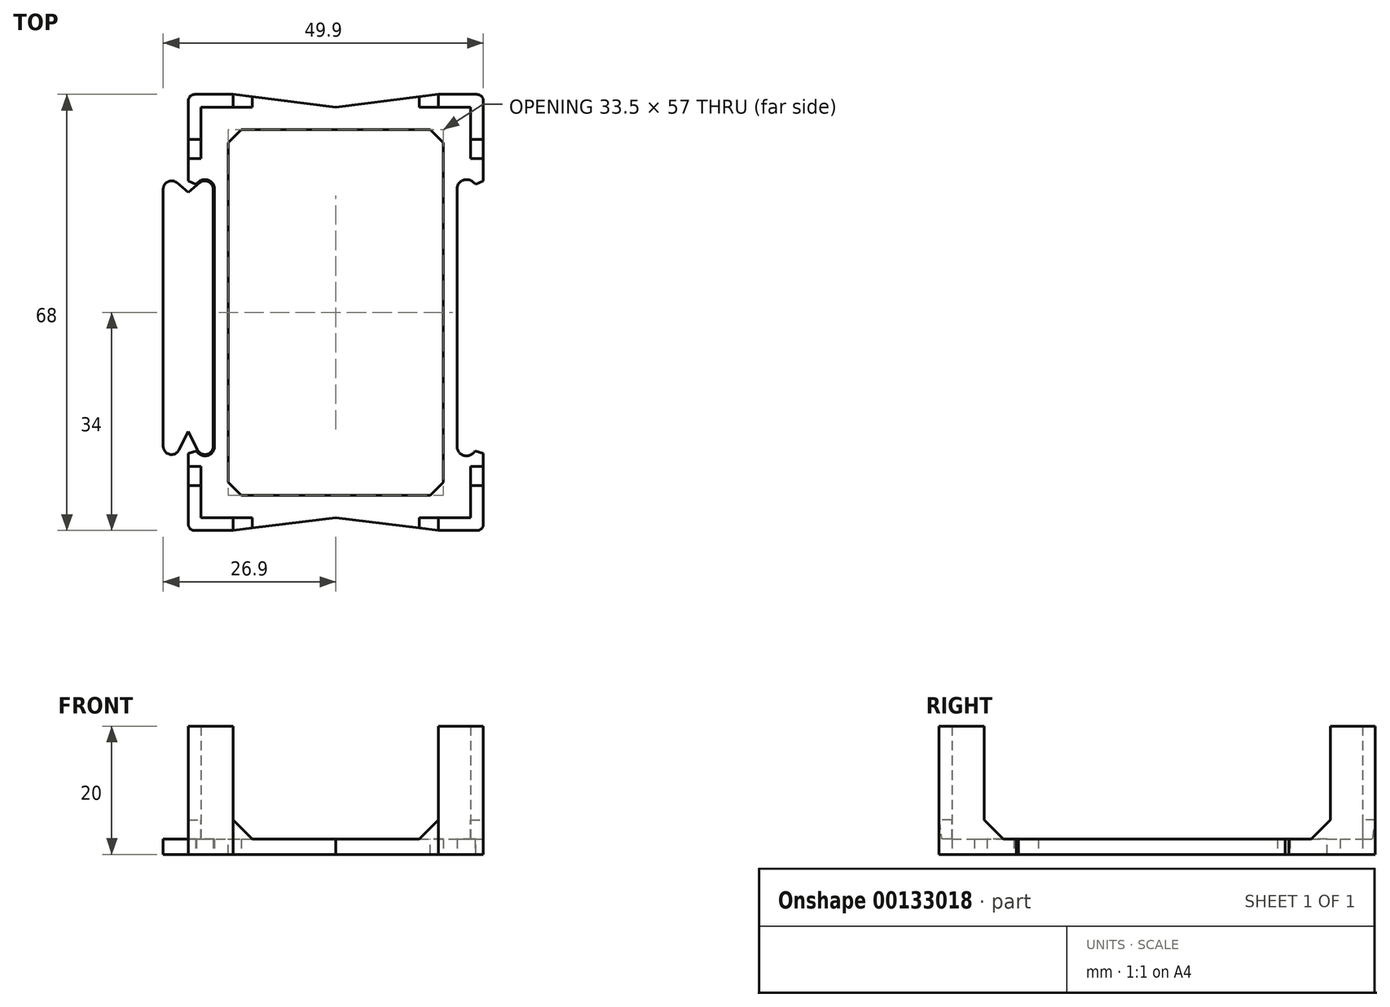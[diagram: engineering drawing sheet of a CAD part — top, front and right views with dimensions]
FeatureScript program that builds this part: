
annotation { "Feature Type Name" : "Feature", "Feature Type Description" : "" }
export const myFeature = defineFeature(function(context is Context, id is Id, definition is map)
    precondition{}
    {
        {
            var Q0;
            Q0=qCreatedBy(makeId("Top.planeOp"),FACE);
            var sketch = newSketch(context, id + "F0", { "sketchPlane" : qUnion([Q0])});
            skLineSegment(sketch, "E0.bottom", {"start": v(21, 32) * mm, "end": v(16, 32) * mm});
            skLineSegment(sketch, "E0.top", {"start": v(21, -32) * mm, "end": v(16, -32) * mm});
            skLineSegment(sketch, "E0.left", {"start": v(21, 32) * mm, "end": v(21, 27) * mm});
            skLineSegment(sketch, "E0.right", {"start": v(-21, 32) * mm, "end": v(-21, 27) * mm});
            skLineSegment(sketch, "E1", {"start": v(-16, 34) * mm, "end": v(-23, 34) * mm});
            skLineSegment(sketch, "E2", {"start": v(-23, 34) * mm, "end": v(-23, 27) * mm});
            skLineSegment(sketch, "E3", {"start": v(-16, 32) * mm, "end": v(-16, 34) * mm});
            skLineSegment(sketch, "E4", {"start": v(-21, 27) * mm, "end": v(-23, 27) * mm});
            skLineSegment(sketch, "E5", {"start": v(16, 34) * mm, "end": v(16, 32) * mm});
            skLineSegment(sketch, "E6", {"start": v(16, 34) * mm, "end": v(23, 34) * mm});
            skLineSegment(sketch, "E7", {"start": v(23, 27) * mm, "end": v(23, 34) * mm});
            skLineSegment(sketch, "E8", {"start": v(21, 27) * mm, "end": v(23, 27) * mm});
            skLineSegment(sketch, "E9", {"start": v(-23, -27) * mm, "end": v(-21, -27) * mm});
            skLineSegment(sketch, "E10", {"start": v(-23, -27) * mm, "end": v(-23, -34) * mm});
            skLineSegment(sketch, "E11", {"start": v(-16, -34) * mm, "end": v(-23, -34) * mm});
            skLineSegment(sketch, "E12", {"start": v(-16, -32) * mm, "end": v(-16, -34) * mm});
            skLineSegment(sketch, "E13", {"start": v(16, -32) * mm, "end": v(16, -34) * mm});
            skLineSegment(sketch, "E14", {"start": v(16, -34) * mm, "end": v(23, -34) * mm});
            skLineSegment(sketch, "E15", {"start": v(23, -27) * mm, "end": v(23, -34) * mm});
            skLineSegment(sketch, "E16", {"start": v(21, -27) * mm, "end": v(23, -27) * mm});
            skLineSegment(sketch, "E17", {"start": v(-16.75, 28.5) * mm, "end": v(16.75, 28.5) * mm});
            skLineSegment(sketch, "E18", {"start": v(16.75, -28.5) * mm, "end": v(-16.75, -28.5) * mm});
            skLineSegment(sketch, "E19", {"start": v(-16.75, 28.5) * mm, "end": v(-16.75, -28.5) * mm});
            skLineSegment(sketch, "E20", {"start": v(16.75, 28.5) * mm, "end": v(16.75, -28.5) * mm});
            skLineSegment(sketch, "E21", {"start": v(-16, 34) * mm, "end": v(0, 32) * mm});
            skLineSegment(sketch, "E22", {"start": v(0, 32) * mm, "end": v(16, 34) * mm});
            skLineSegment(sketch, "E23", {"start": v(-16, -34) * mm, "end": v(0, -32) * mm});
            skLineSegment(sketch, "E24", {"start": v(0, -32) * mm, "end": v(16, -34) * mm});
            skLineSegment(sketch, "E25.trimOffspring", {"start": v(21, -27) * mm, "end": v(21, -32) * mm});
            skLineSegment(sketch, "E26.trimOffspring", {"start": v(-16, -32) * mm, "end": v(-21, -32) * mm});
            skLineSegment(sketch, "E27.trimOffspring", {"start": v(-21, -27) * mm, "end": v(-21, -32) * mm});
            skLineSegment(sketch, "E28", {"start": v(-16, 32) * mm, "end": v(-21, 32) * mm});
            skPoint(sketch, "E29", {"position": v(0, 28.5) * mm});
            skPoint(sketch, "E30", {"position": v(0, -28.5) * mm});
            skPoint(sketch, "E31", {"position": v(-16.75, 0) * mm});
            skPoint(sketch, "E32", {"position": v(16.75, 0) * mm});
            skLineSegment(sketch, "E33", {"start": v(-23, 27) * mm, "end": v(-23, -27) * mm});
            skLineSegment(sketch, "E34", {"start": v(23, -27) * mm, "end": v(23, 27) * mm});
            skLineSegment(sketch, "E35", {"start": v(-23, 19) * mm, "end": v(-21.36, 20.37) * mm});
            skLineSegment(sketch, "E36", {"start": v(-18.9, 19.22) * mm, "end": v(-18.9, -20.86) * mm});
            skLineSegment(sketch, "E37", {"start": v(-21.74, -21.53) * mm, "end": v(-23, -19) * mm});
            skPoint(sketch, "E38.visualSharp", {"position": v(-18.9, 22.44) * mm});
            skArc(sketch, "E38.filletArc", {"start": v(-18.9, 19.22) * mm, "mid": v(-19.76, 20.58) * mm, "end": v(-21.36, 20.37) * mm});
            skPoint(sketch, "E39.visualSharp", {"position": v(-18.9, -27.23) * mm});
            skArc(sketch, "E39.filletArc", {"start": v(-21.74, -21.53) * mm, "mid": v(-20.06, -22.32) * mm, "end": v(-18.9, -20.86) * mm});
            skLineSegment(sketch, "E40.MirrorCS", {"start": v(-23, 19) * mm, "end": v(-24.64, 20.37) * mm});
            skArc(sketch, "E41.MirrorCS", {"start": v(-27.1, 19.22) * mm, "mid": v(-26.24, 20.58) * mm, "end": v(-24.64, 20.37) * mm});
            skLineSegment(sketch, "E42.MirrorCS", {"start": v(-27.1, 19.22) * mm, "end": v(-27.1, -20.86) * mm});
            skArc(sketch, "E43.MirrorCS", {"start": v(-24.26, -21.53) * mm, "mid": v(-25.94, -22.32) * mm, "end": v(-27.1, -20.86) * mm});
            skLineSegment(sketch, "E44.MirrorCS", {"start": v(-24.26, -21.53) * mm, "end": v(-23, -19) * mm});
            skLineSegment(sketch, "E45", {"start": v(0, 40.79) * mm, "end": v(0, -39.35) * mm, "construction": true});
            skLineSegment(sketch, "E46.MirrorCS", {"start": v(18.9, 19.22) * mm, "end": v(18.9, -20.86) * mm});
            skArc(sketch, "E47.MirrorCS", {"start": v(18.9, 19.22) * mm, "mid": v(19.76, 20.58) * mm, "end": v(21.36, 20.37) * mm});
            skLineSegment(sketch, "E48.MirrorCS", {"start": v(23, 19) * mm, "end": v(21.36, 20.37) * mm});
            skLineSegment(sketch, "E49.MirrorCS", {"start": v(23, 19) * mm, "end": v(24.64, 20.37) * mm});
            skArc(sketch, "E50.MirrorCS", {"start": v(27.1, 19.22) * mm, "mid": v(26.24, 20.58) * mm, "end": v(24.64, 20.37) * mm});
            skLineSegment(sketch, "E51.MirrorCS", {"start": v(27.1, 19.22) * mm, "end": v(27.1, -20.86) * mm});
            skArc(sketch, "E52.MirrorCS", {"start": v(24.26, -21.53) * mm, "mid": v(25.94, -22.32) * mm, "end": v(27.1, -20.86) * mm});
            skLineSegment(sketch, "E53.MirrorCS", {"start": v(24.26, -21.53) * mm, "end": v(23, -19) * mm});
            skLineSegment(sketch, "E54.MirrorCS", {"start": v(21.74, -21.53) * mm, "end": v(23, -19) * mm});
            skArc(sketch, "E55.MirrorCS", {"start": v(21.74, -21.53) * mm, "mid": v(20.06, -22.32) * mm, "end": v(18.9, -20.86) * mm});
            skArc(sketch, "E56.0", {"start": v(-19.1, 19.22) * mm, "mid": v(-19.85, 20.4) * mm, "end": v(-21.23, 20.22) * mm});
            skLineSegment(sketch, "E56.1", {"start": v(-23, 18.74) * mm, "end": v(-21.23, 20.22) * mm});
            skLineSegment(sketch, "E56.2", {"start": v(-19.1, 19.22) * mm, "end": v(-19.1, -20.86) * mm});
            skLineSegment(sketch, "E56.3", {"start": v(-23, 18.74) * mm, "end": v(-24.77, 20.22) * mm});
            skArc(sketch, "E56.4", {"start": v(-26.9, 19.22) * mm, "mid": v(-26.15, 20.4) * mm, "end": v(-24.77, 20.22) * mm});
            skLineSegment(sketch, "E56.5", {"start": v(-26.9, 19.22) * mm, "end": v(-26.9, -20.86) * mm});
            skArc(sketch, "E56.6", {"start": v(-21.56, -21.44) * mm, "mid": v(-20.1, -22.12) * mm, "end": v(-19.1, -20.86) * mm});
            skLineSegment(sketch, "E56.7", {"start": v(-21.56, -21.44) * mm, "end": v(-23, -18.55) * mm});
            skLineSegment(sketch, "E56.8", {"start": v(-24.44, -21.44) * mm, "end": v(-23, -18.55) * mm});
            skArc(sketch, "E56.9", {"start": v(-24.44, -21.44) * mm, "mid": v(-25.9, -22.12) * mm, "end": v(-26.9, -20.86) * mm});
            skLineSegment(sketch, "E57.0", {"start": v(-23.9, 19.22) * mm, "end": v(-23.9, -20.86) * mm});
            skSolve(sketch);
        }
        {
            var Q0;
            {var subQ0=sQuery(id+"F0.wireOp",EDGE,"E0.left");var subQ3=sQuery(id+"F0.wireOp",EDGE,"E0.bottom");var subQ4=makeQuery(id+"F0.imprint","INTERSECT",VERTEX,{"derivedFrom":[subQ3,subQ0]});Q0=makeQuery(id+"F0.imprint","IMPRINT",FACE,{"disambiguationData":[TD([[makeQuery(id+"F0.imprint","IMPRINT",EDGE,{"disambiguationData":[TD([[subQ4,-1.0]])],"derivedFrom":subQ3}),1.0]])]});}
            var Q1;
            {var subQ0=sQuery(id+"F0.wireOp",EDGE,"E5");Q1=makeQuery(id+"F0.imprint","IMPRINT",FACE,{"disambiguationData":[TD([[makeQuery(id+"F0.imprint","IMPRINT",EDGE,{"derivedFrom":subQ0}),-1.0]])]});}
            var Q2;
            {var subQ4=sQuery(id+"F0.wireOp",EDGE,"E5");Q2=makeQuery(id+"F0.imprint","IMPRINT",FACE,{"disambiguationData":[TD([[makeQuery(id+"F0.imprint","IMPRINT",EDGE,{"derivedFrom":subQ4}),1.0]])]});}
            var Q3;
            {var subQ0=sQuery(id+"F0.wireOp",EDGE,"E8");Q3=makeQuery(id+"F0.imprint","IMPRINT",FACE,{"disambiguationData":[TD([[makeQuery(id+"F0.imprint","IMPRINT",EDGE,{"derivedFrom":subQ0}),-1.0]])]});}
            var Q4;
            {var subQ0=sQuery(id+"F0.wireOp",EDGE,"E16");Q4=makeQuery(id+"F0.imprint","IMPRINT",FACE,{"disambiguationData":[TD([[makeQuery(id+"F0.imprint","IMPRINT",EDGE,{"derivedFrom":subQ0}),1.0]])]});}
            var Q5;
            {var subQ0=sQuery(id+"F0.wireOp",EDGE,"E13");Q5=makeQuery(id+"F0.imprint","IMPRINT",FACE,{"disambiguationData":[TD([[makeQuery(id+"F0.imprint","IMPRINT",EDGE,{"derivedFrom":subQ0}),1.0]])]});}
            var Q6;
            {var subQ0=sQuery(id+"F0.wireOp",EDGE,"E13");Q6=makeQuery(id+"F0.imprint","IMPRINT",FACE,{"disambiguationData":[TD([[makeQuery(id+"F0.imprint","IMPRINT",EDGE,{"derivedFrom":subQ0}),-1.0]])]});}
            var Q7;
            {var subQ0=sQuery(id+"F0.wireOp",EDGE,"E12");Q7=makeQuery(id+"F0.imprint","IMPRINT",FACE,{"disambiguationData":[TD([[makeQuery(id+"F0.imprint","IMPRINT",EDGE,{"derivedFrom":subQ0}),1.0]])]});}
            var Q8;
            {var subQ4=sQuery(id+"F0.wireOp",EDGE,"E9");Q8=makeQuery(id+"F0.imprint","IMPRINT",FACE,{"disambiguationData":[TD([[makeQuery(id+"F0.imprint","IMPRINT",EDGE,{"derivedFrom":subQ4}),-1.0]])]});}
            var Q9;
            {var subQ0=sQuery(id+"F0.wireOp",EDGE,"E9");Q9=makeQuery(id+"F0.imprint","IMPRINT",FACE,{"disambiguationData":[TD([[makeQuery(id+"F0.imprint","IMPRINT",EDGE,{"derivedFrom":subQ0}),1.0]])]});}
            var Q10;
            {var subQ0=sQuery(id+"F0.wireOp",EDGE,"E4");Q10=makeQuery(id+"F0.imprint","IMPRINT",FACE,{"disambiguationData":[TD([[makeQuery(id+"F0.imprint","IMPRINT",EDGE,{"derivedFrom":subQ0}),1.0]])]});}
            var Q11;
            Q11=makeQuery(id+"F0.imprint","IMPRINT",FACE,{"disambiguationData":[TD([[makeQuery(id+"F0.imprint","IMPRINT",EDGE,{"derivedFrom":sQuery(id+"F0.wireOp",EDGE,"E1")}),1.0]])]});
            var Q12;
            {var subQ0=sQuery(id+"F0.wireOp",EDGE,"E3");Q12=makeQuery(id+"F0.imprint","IMPRINT",FACE,{"disambiguationData":[TD([[makeQuery(id+"F0.imprint","IMPRINT",EDGE,{"derivedFrom":subQ0}),-1.0]])]});}
            extrude(context, id + "F1", {"entities" : qUnion([Q0, Q1, Q2, Q3, Q4, Q5, Q6, Q7, Q8, Q9, Q10, Q11, Q12]), "depth" : 2.4 * mm});
        }
        {
            var Q0;
            Q0=makeQuery(id+"F0.imprint","IMPRINT",FACE,{"disambiguationData":[TD([[makeQuery(id+"F0.imprint","IMPRINT",EDGE,{"derivedFrom":sQuery(id+"F0.wireOp",EDGE,"E1")}),1.0]])]});
            var Q1;
            {var subQ4=sQuery(id+"F0.wireOp",EDGE,"E5");Q1=makeQuery(id+"F0.imprint","IMPRINT",FACE,{"disambiguationData":[TD([[makeQuery(id+"F0.imprint","IMPRINT",EDGE,{"derivedFrom":subQ4}),1.0]])]});}
            var Q2;
            {var subQ0=sQuery(id+"F0.wireOp",EDGE,"E13");Q2=makeQuery(id+"F0.imprint","IMPRINT",FACE,{"disambiguationData":[TD([[makeQuery(id+"F0.imprint","IMPRINT",EDGE,{"derivedFrom":subQ0}),1.0]])]});}
            var Q3;
            {var subQ3=sQuery(id+"F0.wireOp",EDGE,"E9");Q3=makeQuery(id+"F0.imprint","IMPRINT",FACE,{"disambiguationData":[TD([[makeQuery(id+"F0.imprint","IMPRINT",EDGE,{"derivedFrom":subQ3}),-1.0]])]});}
            extrude(context, id + "F2", {"entities" : qUnion([Q0, Q1, Q2, Q3]), "operationType" : NewBodyOperationType.ADD, "depth" : 20 * mm});
        }
        {
            var Q0;
            Q0=makeQuery(id+"F2.boolean.opBoolean","INTERSECT",EDGE,{"derivedFrom":[makeQuery(id+"F1.opExtrude","CAP_FACE",FACE,{"disambiguationData":[OSD([sQuery(id+"F0.wireOp",EDGE,"E1"),sQuery(id+"F0.wireOp",EDGE,"E2"),sQuery(id+"F0.wireOp",EDGE,"E6"),sQuery(id+"F0.wireOp",EDGE,"E7"),sQuery(id+"F0.wireOp",EDGE,"E10"),sQuery(id+"F0.wireOp",EDGE,"E11"),sQuery(id+"F0.wireOp",EDGE,"E14"),sQuery(id+"F0.wireOp",EDGE,"E15"),sQuery(id+"F0.wireOp",EDGE,"E17"),sQuery(id+"F0.wireOp",EDGE,"E18"),sQuery(id+"F0.wireOp",EDGE,"E19"),sQuery(id+"F0.wireOp",EDGE,"E20"),sQuery(id+"F0.wireOp",EDGE,"jiaWZDtS-R24L-EVNI-qtd6-zTstN88FOwR1"),sQuery(id+"F0.wireOp",EDGE,"sGljjnvT-gn0O-4xuL-FiDi-xVXoTiZH4aIa"),sQuery(id+"F0.wireOp",EDGE,"JoJTnnvT-VXK7-kJcO-3MJ3-lJnIAB2w7SyZ"),sQuery(id+"F0.wireOp",EDGE,"D99VeNCh-oXrI-DHgS-fi0i-UPG9c3mJZdQb"),sQuery(id+"F0.wireOp",EDGE,"E21"),sQuery(id+"F0.wireOp",EDGE,"E22"),sQuery(id+"F0.wireOp",EDGE,"E23"),sQuery(id+"F0.wireOp",EDGE,"E24")])],"isStart":false}),makeQuery(id+"F2.opExtrude","SWEPT_FACE",FACE,{"disambiguationData":[OSD([sQuery(id+"F0.wireOp",EDGE,"E4")])]})]});
            var Q1;
            Q1=makeQuery(id+"F2.boolean.opBoolean","INTERSECT",EDGE,{"derivedFrom":[makeQuery(id+"F1.opExtrude","CAP_FACE",FACE,{"disambiguationData":[OSD([sQuery(id+"F0.wireOp",EDGE,"E1"),sQuery(id+"F0.wireOp",EDGE,"E2"),sQuery(id+"F0.wireOp",EDGE,"E6"),sQuery(id+"F0.wireOp",EDGE,"E7"),sQuery(id+"F0.wireOp",EDGE,"E10"),sQuery(id+"F0.wireOp",EDGE,"E11"),sQuery(id+"F0.wireOp",EDGE,"E14"),sQuery(id+"F0.wireOp",EDGE,"E15"),sQuery(id+"F0.wireOp",EDGE,"E17"),sQuery(id+"F0.wireOp",EDGE,"E18"),sQuery(id+"F0.wireOp",EDGE,"E19"),sQuery(id+"F0.wireOp",EDGE,"E20"),sQuery(id+"F0.wireOp",EDGE,"jiaWZDtS-R24L-EVNI-qtd6-zTstN88FOwR1"),sQuery(id+"F0.wireOp",EDGE,"sGljjnvT-gn0O-4xuL-FiDi-xVXoTiZH4aIa"),sQuery(id+"F0.wireOp",EDGE,"JoJTnnvT-VXK7-kJcO-3MJ3-lJnIAB2w7SyZ"),sQuery(id+"F0.wireOp",EDGE,"D99VeNCh-oXrI-DHgS-fi0i-UPG9c3mJZdQb"),sQuery(id+"F0.wireOp",EDGE,"E21"),sQuery(id+"F0.wireOp",EDGE,"E22"),sQuery(id+"F0.wireOp",EDGE,"E23"),sQuery(id+"F0.wireOp",EDGE,"E24")])],"isStart":false}),makeQuery(id+"F2.opExtrude","SWEPT_FACE",FACE,{"disambiguationData":[OSD([sQuery(id+"F0.wireOp",EDGE,"E3")])]})]});
            var Q2;
            Q2=makeQuery(id+"F2.boolean.opBoolean","INTERSECT",EDGE,{"derivedFrom":[makeQuery(id+"F1.opExtrude","CAP_FACE",FACE,{"disambiguationData":[OSD([sQuery(id+"F0.wireOp",EDGE,"E1"),sQuery(id+"F0.wireOp",EDGE,"E2"),sQuery(id+"F0.wireOp",EDGE,"E6"),sQuery(id+"F0.wireOp",EDGE,"E7"),sQuery(id+"F0.wireOp",EDGE,"E10"),sQuery(id+"F0.wireOp",EDGE,"E11"),sQuery(id+"F0.wireOp",EDGE,"E14"),sQuery(id+"F0.wireOp",EDGE,"E15"),sQuery(id+"F0.wireOp",EDGE,"E17"),sQuery(id+"F0.wireOp",EDGE,"E18"),sQuery(id+"F0.wireOp",EDGE,"E19"),sQuery(id+"F0.wireOp",EDGE,"E20"),sQuery(id+"F0.wireOp",EDGE,"jiaWZDtS-R24L-EVNI-qtd6-zTstN88FOwR1"),sQuery(id+"F0.wireOp",EDGE,"sGljjnvT-gn0O-4xuL-FiDi-xVXoTiZH4aIa"),sQuery(id+"F0.wireOp",EDGE,"JoJTnnvT-VXK7-kJcO-3MJ3-lJnIAB2w7SyZ"),sQuery(id+"F0.wireOp",EDGE,"D99VeNCh-oXrI-DHgS-fi0i-UPG9c3mJZdQb"),sQuery(id+"F0.wireOp",EDGE,"E21"),sQuery(id+"F0.wireOp",EDGE,"E22"),sQuery(id+"F0.wireOp",EDGE,"E23"),sQuery(id+"F0.wireOp",EDGE,"E24")])],"isStart":false}),makeQuery(id+"F2.opExtrude","SWEPT_FACE",FACE,{"disambiguationData":[OSD([sQuery(id+"F0.wireOp",EDGE,"E8")])]})]});
            var Q3;
            Q3=makeQuery(id+"F2.boolean.opBoolean","INTERSECT",EDGE,{"derivedFrom":[makeQuery(id+"F1.opExtrude","CAP_FACE",FACE,{"disambiguationData":[OSD([sQuery(id+"F0.wireOp",EDGE,"E1"),sQuery(id+"F0.wireOp",EDGE,"E2"),sQuery(id+"F0.wireOp",EDGE,"E6"),sQuery(id+"F0.wireOp",EDGE,"E7"),sQuery(id+"F0.wireOp",EDGE,"E10"),sQuery(id+"F0.wireOp",EDGE,"E11"),sQuery(id+"F0.wireOp",EDGE,"E14"),sQuery(id+"F0.wireOp",EDGE,"E15"),sQuery(id+"F0.wireOp",EDGE,"E17"),sQuery(id+"F0.wireOp",EDGE,"E18"),sQuery(id+"F0.wireOp",EDGE,"E19"),sQuery(id+"F0.wireOp",EDGE,"E20"),sQuery(id+"F0.wireOp",EDGE,"jiaWZDtS-R24L-EVNI-qtd6-zTstN88FOwR1"),sQuery(id+"F0.wireOp",EDGE,"sGljjnvT-gn0O-4xuL-FiDi-xVXoTiZH4aIa"),sQuery(id+"F0.wireOp",EDGE,"JoJTnnvT-VXK7-kJcO-3MJ3-lJnIAB2w7SyZ"),sQuery(id+"F0.wireOp",EDGE,"D99VeNCh-oXrI-DHgS-fi0i-UPG9c3mJZdQb"),sQuery(id+"F0.wireOp",EDGE,"E21"),sQuery(id+"F0.wireOp",EDGE,"E22"),sQuery(id+"F0.wireOp",EDGE,"E23"),sQuery(id+"F0.wireOp",EDGE,"E24")])],"isStart":false}),makeQuery(id+"F2.opExtrude","SWEPT_FACE",FACE,{"disambiguationData":[OSD([sQuery(id+"F0.wireOp",EDGE,"E5")])]})]});
            var Q4;
            Q4=makeQuery(id+"F2.boolean.opBoolean","INTERSECT",EDGE,{"derivedFrom":[makeQuery(id+"F1.opExtrude","CAP_FACE",FACE,{"disambiguationData":[OSD([sQuery(id+"F0.wireOp",EDGE,"E1"),sQuery(id+"F0.wireOp",EDGE,"E2"),sQuery(id+"F0.wireOp",EDGE,"E6"),sQuery(id+"F0.wireOp",EDGE,"E7"),sQuery(id+"F0.wireOp",EDGE,"E10"),sQuery(id+"F0.wireOp",EDGE,"E11"),sQuery(id+"F0.wireOp",EDGE,"E14"),sQuery(id+"F0.wireOp",EDGE,"E15"),sQuery(id+"F0.wireOp",EDGE,"E17"),sQuery(id+"F0.wireOp",EDGE,"E18"),sQuery(id+"F0.wireOp",EDGE,"E19"),sQuery(id+"F0.wireOp",EDGE,"E20"),sQuery(id+"F0.wireOp",EDGE,"jiaWZDtS-R24L-EVNI-qtd6-zTstN88FOwR1"),sQuery(id+"F0.wireOp",EDGE,"sGljjnvT-gn0O-4xuL-FiDi-xVXoTiZH4aIa"),sQuery(id+"F0.wireOp",EDGE,"JoJTnnvT-VXK7-kJcO-3MJ3-lJnIAB2w7SyZ"),sQuery(id+"F0.wireOp",EDGE,"D99VeNCh-oXrI-DHgS-fi0i-UPG9c3mJZdQb"),sQuery(id+"F0.wireOp",EDGE,"E21"),sQuery(id+"F0.wireOp",EDGE,"E22"),sQuery(id+"F0.wireOp",EDGE,"E23"),sQuery(id+"F0.wireOp",EDGE,"E24")])],"isStart":false}),makeQuery(id+"F2.opExtrude","SWEPT_FACE",FACE,{"disambiguationData":[OSD([sQuery(id+"F0.wireOp",EDGE,"E12")])]})]});
            var Q5;
            Q5=makeQuery(id+"F2.boolean.opBoolean","INTERSECT",EDGE,{"derivedFrom":[makeQuery(id+"F1.opExtrude","CAP_FACE",FACE,{"disambiguationData":[OSD([sQuery(id+"F0.wireOp",EDGE,"E1"),sQuery(id+"F0.wireOp",EDGE,"E2"),sQuery(id+"F0.wireOp",EDGE,"E6"),sQuery(id+"F0.wireOp",EDGE,"E7"),sQuery(id+"F0.wireOp",EDGE,"E10"),sQuery(id+"F0.wireOp",EDGE,"E11"),sQuery(id+"F0.wireOp",EDGE,"E14"),sQuery(id+"F0.wireOp",EDGE,"E15"),sQuery(id+"F0.wireOp",EDGE,"E17"),sQuery(id+"F0.wireOp",EDGE,"E18"),sQuery(id+"F0.wireOp",EDGE,"E19"),sQuery(id+"F0.wireOp",EDGE,"E20"),sQuery(id+"F0.wireOp",EDGE,"jiaWZDtS-R24L-EVNI-qtd6-zTstN88FOwR1"),sQuery(id+"F0.wireOp",EDGE,"sGljjnvT-gn0O-4xuL-FiDi-xVXoTiZH4aIa"),sQuery(id+"F0.wireOp",EDGE,"JoJTnnvT-VXK7-kJcO-3MJ3-lJnIAB2w7SyZ"),sQuery(id+"F0.wireOp",EDGE,"D99VeNCh-oXrI-DHgS-fi0i-UPG9c3mJZdQb"),sQuery(id+"F0.wireOp",EDGE,"E21"),sQuery(id+"F0.wireOp",EDGE,"E22"),sQuery(id+"F0.wireOp",EDGE,"E23"),sQuery(id+"F0.wireOp",EDGE,"E24")])],"isStart":false}),makeQuery(id+"F2.opExtrude","SWEPT_FACE",FACE,{"disambiguationData":[OSD([sQuery(id+"F0.wireOp",EDGE,"E9")])]})]});
            var Q6;
            Q6=makeQuery(id+"F2.boolean.opBoolean","INTERSECT",EDGE,{"derivedFrom":[makeQuery(id+"F1.opExtrude","CAP_FACE",FACE,{"disambiguationData":[OSD([sQuery(id+"F0.wireOp",EDGE,"E1"),sQuery(id+"F0.wireOp",EDGE,"E2"),sQuery(id+"F0.wireOp",EDGE,"E6"),sQuery(id+"F0.wireOp",EDGE,"E7"),sQuery(id+"F0.wireOp",EDGE,"E10"),sQuery(id+"F0.wireOp",EDGE,"E11"),sQuery(id+"F0.wireOp",EDGE,"E14"),sQuery(id+"F0.wireOp",EDGE,"E15"),sQuery(id+"F0.wireOp",EDGE,"E17"),sQuery(id+"F0.wireOp",EDGE,"E18"),sQuery(id+"F0.wireOp",EDGE,"E19"),sQuery(id+"F0.wireOp",EDGE,"E20"),sQuery(id+"F0.wireOp",EDGE,"jiaWZDtS-R24L-EVNI-qtd6-zTstN88FOwR1"),sQuery(id+"F0.wireOp",EDGE,"sGljjnvT-gn0O-4xuL-FiDi-xVXoTiZH4aIa"),sQuery(id+"F0.wireOp",EDGE,"JoJTnnvT-VXK7-kJcO-3MJ3-lJnIAB2w7SyZ"),sQuery(id+"F0.wireOp",EDGE,"D99VeNCh-oXrI-DHgS-fi0i-UPG9c3mJZdQb"),sQuery(id+"F0.wireOp",EDGE,"E21"),sQuery(id+"F0.wireOp",EDGE,"E22"),sQuery(id+"F0.wireOp",EDGE,"E23"),sQuery(id+"F0.wireOp",EDGE,"E24")])],"isStart":false}),makeQuery(id+"F2.opExtrude","SWEPT_FACE",FACE,{"disambiguationData":[OSD([sQuery(id+"F0.wireOp",EDGE,"E16")])]})]});
            var Q7;
            Q7=makeQuery(id+"F2.boolean.opBoolean","INTERSECT",EDGE,{"derivedFrom":[makeQuery(id+"F1.opExtrude","CAP_FACE",FACE,{"disambiguationData":[OSD([sQuery(id+"F0.wireOp",EDGE,"E1"),sQuery(id+"F0.wireOp",EDGE,"E2"),sQuery(id+"F0.wireOp",EDGE,"E6"),sQuery(id+"F0.wireOp",EDGE,"E7"),sQuery(id+"F0.wireOp",EDGE,"E10"),sQuery(id+"F0.wireOp",EDGE,"E11"),sQuery(id+"F0.wireOp",EDGE,"E14"),sQuery(id+"F0.wireOp",EDGE,"E15"),sQuery(id+"F0.wireOp",EDGE,"E17"),sQuery(id+"F0.wireOp",EDGE,"E18"),sQuery(id+"F0.wireOp",EDGE,"E19"),sQuery(id+"F0.wireOp",EDGE,"E20"),sQuery(id+"F0.wireOp",EDGE,"jiaWZDtS-R24L-EVNI-qtd6-zTstN88FOwR1"),sQuery(id+"F0.wireOp",EDGE,"sGljjnvT-gn0O-4xuL-FiDi-xVXoTiZH4aIa"),sQuery(id+"F0.wireOp",EDGE,"JoJTnnvT-VXK7-kJcO-3MJ3-lJnIAB2w7SyZ"),sQuery(id+"F0.wireOp",EDGE,"D99VeNCh-oXrI-DHgS-fi0i-UPG9c3mJZdQb"),sQuery(id+"F0.wireOp",EDGE,"E21"),sQuery(id+"F0.wireOp",EDGE,"E22"),sQuery(id+"F0.wireOp",EDGE,"E23"),sQuery(id+"F0.wireOp",EDGE,"E24")])],"isStart":false}),makeQuery(id+"F2.opExtrude","SWEPT_FACE",FACE,{"disambiguationData":[OSD([sQuery(id+"F0.wireOp",EDGE,"E13")])]})]});
            chamfer(context, id + "F3", {"entities" : qUnion([Q0, Q1, Q2, Q3, Q4, Q5, Q6, Q7]), "width" : 3 * mm, "tangentPropagation" : true});
        }
        {
            var Q0;
            Q0=makeQuery(id+"F1.opExtrude","SWEPT_EDGE",EDGE,{"disambiguationData":[OSD([sQuery(id+"F0.wireOp",EDGE,"E17"),sQuery(id+"F0.wireOp",EDGE,"E19")])]});
            var Q1;
            Q1=makeQuery(id+"F1.opExtrude","SWEPT_EDGE",EDGE,{"disambiguationData":[OSD([sQuery(id+"F0.wireOp",EDGE,"E17"),sQuery(id+"F0.wireOp",EDGE,"E20")])]});
            var Q2;
            Q2=makeQuery(id+"F1.opExtrude","SWEPT_EDGE",EDGE,{"disambiguationData":[OSD([sQuery(id+"F0.wireOp",EDGE,"E18"),sQuery(id+"F0.wireOp",EDGE,"E19")])]});
            var Q3;
            Q3=makeQuery(id+"F1.opExtrude","SWEPT_EDGE",EDGE,{"disambiguationData":[OSD([sQuery(id+"F0.wireOp",EDGE,"E18"),sQuery(id+"F0.wireOp",EDGE,"E20")])]});
            chamfer(context, id + "F4", {"entities" : qUnion([Q0, Q1, Q2, Q3]), "width" : 2 * mm, "tangentPropagation" : true});
        }
        {
            var Q0;
            Q0=makeQuery(id+"F0.imprint","IMPRINT",FACE,{"disambiguationData":[TD([[makeQuery(id+"F0.imprint","IMPRINT",EDGE,{"derivedFrom":sQuery(id+"F0.wireOp",EDGE,"E56.0")}),1.0]])]});
            var Q1;
            {var subQ0=sQuery(id+"F0.wireOp",EDGE,"E56.3");Q1=makeQuery(id+"F0.imprint","IMPRINT",FACE,{"disambiguationData":[TD([[makeQuery(id+"F0.imprint","IMPRINT",EDGE,{"derivedFrom":subQ0}),1.0]])]});}
            extrude(context, id + "F5", {"entities" : qUnion([Q0, Q1]), "depth" : 2.4 * mm});
        }
        {
            var Q0;
            Q0=makeQuery(id+"F1.opExtrude","SWEPT_EDGE",EDGE,{"disambiguationData":[OSD([sQuery(id+"F0.wireOp",EDGE,"E33"),sQuery(id+"F0.wireOp",EDGE,"E35"),sQuery(id+"F0.wireOp",EDGE,"E40.MirrorCS")])]});
            var Q1;
            Q1=makeQuery(id+"F1.opExtrude","SWEPT_EDGE",EDGE,{"disambiguationData":[OSD([sQuery(id+"F0.wireOp",EDGE,"E33"),sQuery(id+"F0.wireOp",EDGE,"E37"),sQuery(id+"F0.wireOp",EDGE,"E44.MirrorCS")])]});
            var Q2;
            Q2=makeQuery(id+"F1.opExtrude","SWEPT_EDGE",EDGE,{"disambiguationData":[OSD([sQuery(id+"F0.wireOp",EDGE,"E34"),sQuery(id+"F0.wireOp",EDGE,"E48.MirrorCS"),sQuery(id+"F0.wireOp",EDGE,"E49.MirrorCS")])]});
            var Q3;
            Q3=makeQuery(id+"F1.opExtrude","SWEPT_EDGE",EDGE,{"disambiguationData":[OSD([sQuery(id+"F0.wireOp",EDGE,"E34"),sQuery(id+"F0.wireOp",EDGE,"E53.MirrorCS"),sQuery(id+"F0.wireOp",EDGE,"E54.MirrorCS")])]});
            chamfer(context, id + "F6", {"entities" : qUnion([Q0, Q1, Q2, Q3]), "width" : .7 * mm, "tangentPropagation" : true});
        }
        {
            var Q0;
            {var subQ0=sQuery(id+"F0.wireOp",EDGE,"E11");var subQ1=sQuery(id+"F0.wireOp",EDGE,"E10");Q0=makeQuery(id+"F2.boolean.opBoolean","MERGE",EDGE,{"derivedFrom":[makeQuery(id+"F1.opExtrude","SWEPT_EDGE",EDGE,{"disambiguationData":[OSD([subQ1,subQ0])]}),makeQuery(id+"F2.opExtrude","SWEPT_EDGE",EDGE,{"disambiguationData":[OSD([subQ1,subQ0])]})]});}
            var Q1;
            {var subQ0=sQuery(id+"F0.wireOp",EDGE,"E15");var subQ1=sQuery(id+"F0.wireOp",EDGE,"E14");Q1=makeQuery(id+"F2.boolean.opBoolean","MERGE",EDGE,{"derivedFrom":[makeQuery(id+"F1.opExtrude","SWEPT_EDGE",EDGE,{"disambiguationData":[OSD([subQ1,subQ0])]}),makeQuery(id+"F2.opExtrude","SWEPT_EDGE",EDGE,{"disambiguationData":[OSD([subQ1,subQ0])]})]});}
            var Q2;
            {var subQ0=sQuery(id+"F0.wireOp",EDGE,"E7");var subQ1=sQuery(id+"F0.wireOp",EDGE,"E6");Q2=makeQuery(id+"F2.boolean.opBoolean","MERGE",EDGE,{"derivedFrom":[makeQuery(id+"F1.opExtrude","SWEPT_EDGE",EDGE,{"disambiguationData":[OSD([subQ1,subQ0])]}),makeQuery(id+"F2.opExtrude","SWEPT_EDGE",EDGE,{"disambiguationData":[OSD([subQ1,subQ0])]})]});}
            var Q3;
            {var subQ0=sQuery(id+"F0.wireOp",EDGE,"E2");var subQ1=sQuery(id+"F0.wireOp",EDGE,"E1");Q3=makeQuery(id+"F2.boolean.opBoolean","MERGE",EDGE,{"derivedFrom":[makeQuery(id+"F1.opExtrude","SWEPT_EDGE",EDGE,{"disambiguationData":[OSD([subQ1,subQ0])]}),makeQuery(id+"F2.opExtrude","SWEPT_EDGE",EDGE,{"disambiguationData":[OSD([subQ1,subQ0])]})]});}
            fillet(context, id + "F7", {"entities" : qUnion([Q0, Q1, Q2, Q3]), "radius" : 1 * mm, "tangentPropagation" : true, "allowEdgeOverflow" : false});
        }
    });
